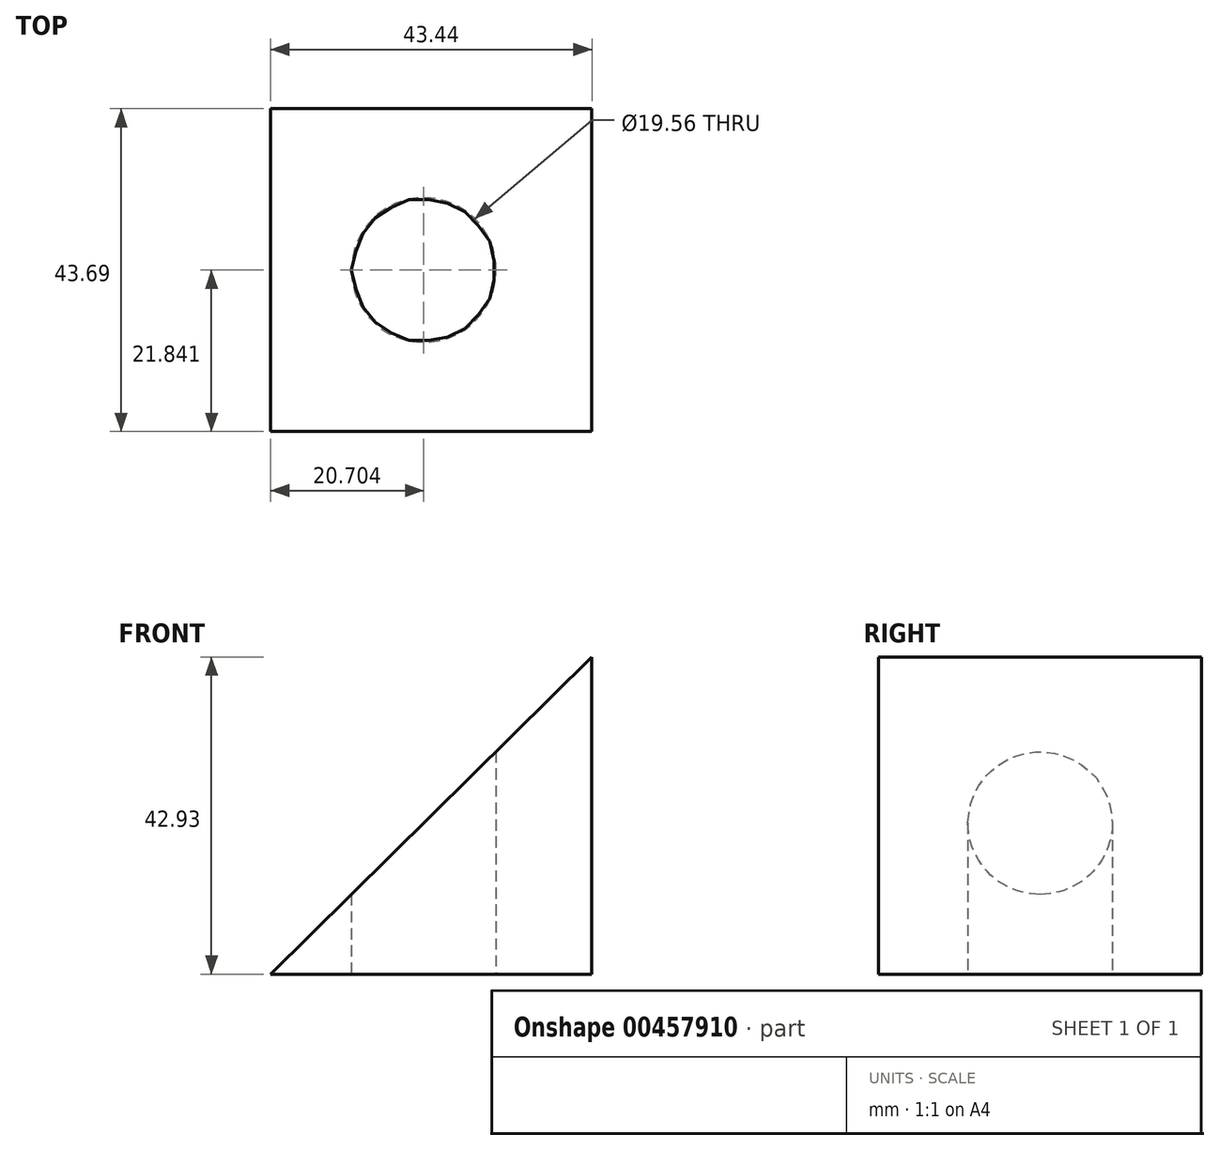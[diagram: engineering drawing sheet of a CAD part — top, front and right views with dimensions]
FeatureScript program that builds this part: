
annotation { "Feature Type Name" : "Feature", "Feature Type Description" : "" }
export const myFeature = defineFeature(function(context is Context, id is Id, definition is map)
    precondition{}
    {
        {
            var Q0;
            Q0=qCreatedBy(makeId("Top.planeOp"),FACE);
            var sketch = newSketch(context, id + "F0", { "sketchPlane" : qUnion([Q0])});
            skLineSegment(sketch, "E0.bottom", {"start": v(-19.7, 33.69) * mm, "end": v(23.73, 33.69) * mm});
            skLineSegment(sketch, "E0.top", {"start": v(-19.7, -10) * mm, "end": v(23.73, -10) * mm});
            skLineSegment(sketch, "E0.left", {"start": v(-19.7, 33.69) * mm, "end": v(-19.7, -10) * mm});
            skLineSegment(sketch, "E0.right", {"start": v(23.73, 33.69) * mm, "end": v(23.73, -10) * mm});
            skLineSegment(sketch, "E1", {"start": v(-19.7, 11.84) * mm, "end": v(1, 11.84) * mm, "construction": true});
            skCircle(sketch, "E2", {"center": v(1, 11.84) * mm, "radius": 9.78 * mm});
            skSolve(sketch);
        }
        {
            var Q0;
            Q0=makeQuery(id+"F0.imprint","IMPRINT",FACE,{"disambiguationData":[TD([[makeQuery(id+"F0.imprint","IMPRINT",EDGE,{"derivedFrom":sQuery(id+"F0.wireOp",EDGE,"E0.bottom")}),-1.0]])]});
            extrude(context, id + "F1", {"entities" : qUnion([Q0]), "depth" : 42.93 * mm});
        }
        {
            var Q0;
            Q0=makeQuery(id+"F1.opExtrude","SWEPT_FACE",FACE,{"disambiguationData":[OSD([sQuery(id+"F0.wireOp",EDGE,"E0.top")])]});
            var sketch = newSketch(context, id + "F2", { "sketchPlane" : qUnion([Q0])});
            skLineSegment(sketch, "E3", {"start": v(23.73, 42.93) * mm, "end": v(-19.7, 0) * mm});
            skSolve(sketch);
        }
        {
            var Q0;
            Q0=makeQuery(id+"F2.imprint","IMPRINT",FACE,{"disambiguationData":[TD([[makeQuery(id+"F2.imprint","IMPRINT",EDGE,{"derivedFrom":sQuery(id+"F2.wireOp",EDGE,"E3")}),-1.0]])]});
            extrude(context, id + "F3", {"entities" : qUnion([Q0]), "operationType" : NewBodyOperationType.REMOVE, "endBound" : BoundingType.THROUGH_ALL, "oppositeDirection" : true, "depth" : 25.4 * mm});
        }
    });
